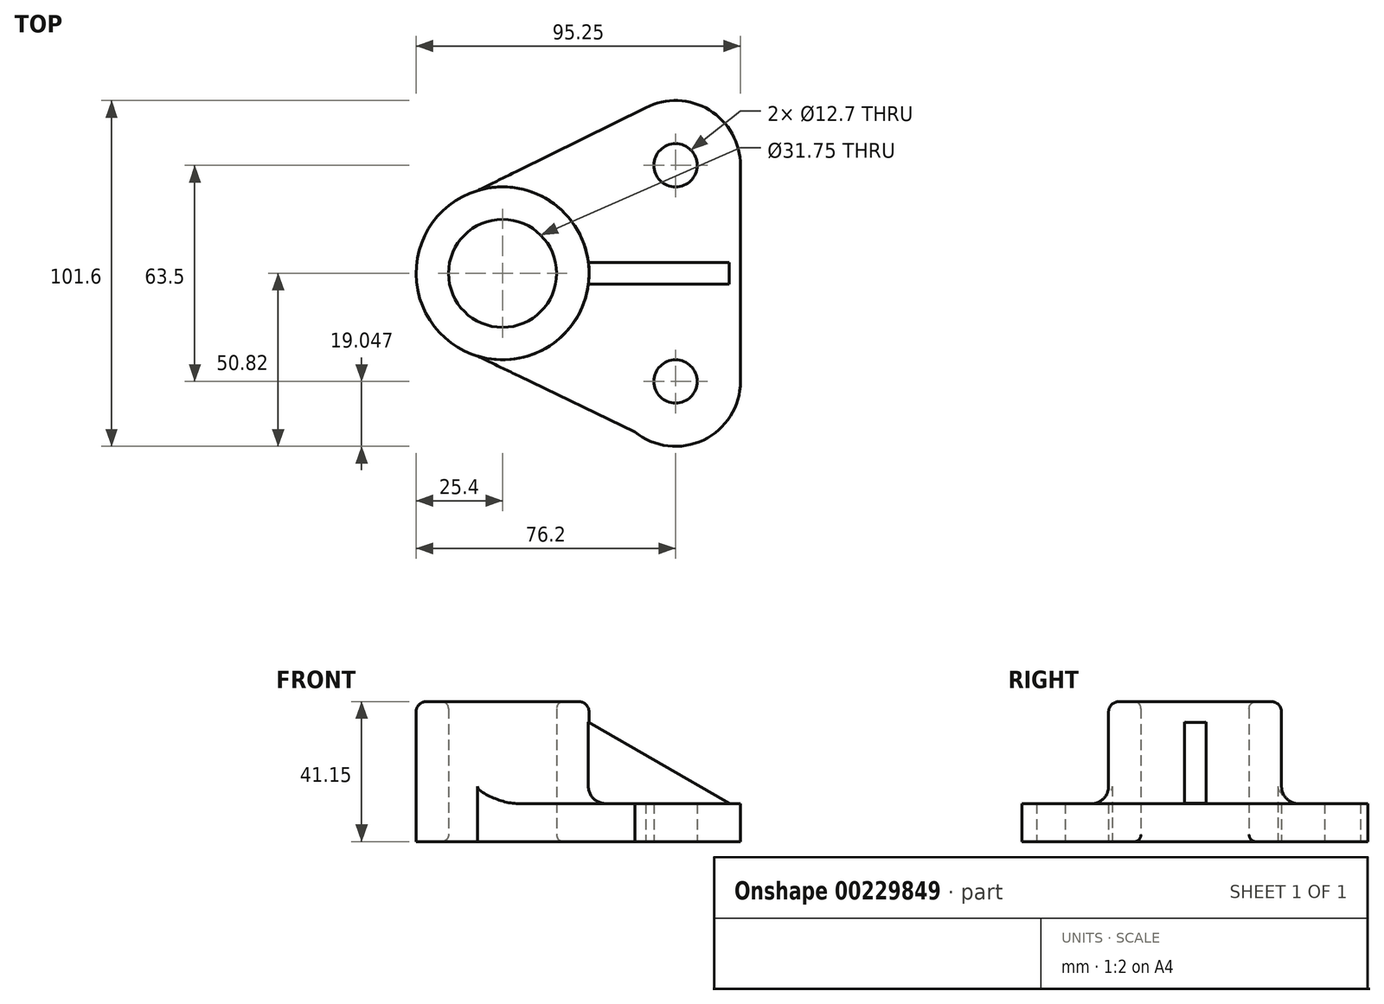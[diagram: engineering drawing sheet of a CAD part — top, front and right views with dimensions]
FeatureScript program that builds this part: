
annotation { "Feature Type Name" : "Feature", "Feature Type Description" : "" }
export const myFeature = defineFeature(function(context is Context, id is Id, definition is map)
    precondition{}
    {
        {
            var Q0;
            Q0=qCreatedBy(makeId("Top.planeOp"),FACE);
            var sketch = newSketch(context, id + "F0", { "sketchPlane" : qUnion([Q0])});
            skCircle(sketch, "E0", {"center": v(-50.8, 0) * mm, "radius": 25.4 * mm});
            skCircle(sketch, "E1", {"center": v(0, 31.73) * mm, "radius": 6.35 * mm});
            skCircle(sketch, "E2", {"center": v(0, -31.77) * mm, "radius": 6.35 * mm});
            skCircle(sketch, "E3", {"center": v(-50.8, 0) * mm, "radius": 15.88 * mm});
            skArc(sketch, "E4", {"start": v(-12.58, 46.03) * mm, "mid": v(15.55, 42.73) * mm, "end": v(9.31, 15.1) * mm});
            skArc(sketch, "E5", {"start": v(-10.88, -16.13) * mm, "mid": v(16.88, -40.6) * mm, "end": v(-19.05, -31.77) * mm});
            skLineSegment(sketch, "E6", {"start": v(19.05, -31.77) * mm, "end": v(19.05, 31.8) * mm});
            skLineSegment(sketch, "E7", {"start": v(-11.99, -46.58) * mm, "end": v(-58.2, -24.3) * mm});
            skLineSegment(sketch, "E8", {"start": v(-8.74, 48.65) * mm, "end": v(-58.2, 24.3) * mm});
            skLineSegment(sketch, "E9", {"start": v(19.05, 0.01) * mm, "end": v(15.75, 0.01) * mm});
            skLineSegment(sketch, "E10", {"start": v(15.75, -3.16) * mm, "end": v(15.75, 3.19) * mm});
            skLineSegment(sketch, "E11", {"start": v(15.75, 3.19) * mm, "end": v(-25.6, 3.19) * mm});
            skLineSegment(sketch, "E12", {"start": v(15.75, -3.16) * mm, "end": v(-25.6, -3.16) * mm});
            skSolve(sketch);
        }
        {
            var Q0;
            Q0=makeQuery(id+"F0.imprint","IMPRINT",FACE,{"disambiguationData":[TD([[makeQuery(id+"F0.imprint","IMPRINT",EDGE,{"derivedFrom":sQuery(id+"F0.wireOp",EDGE,"E0")}),1.0]])]});
            extrude(context, id + "F1", {"entities" : qUnion([Q0]), "depth" : 41.15 * mm});
        }
        {
            var Q0;
            Q0 = qSketchRegion(id + "F0", true);
            extrude(context, id + "F2", {"entities" : qUnion([Q0]), "operationType" : NewBodyOperationType.ADD, "depth" : 11.18 * mm});
        }
        {
            var Q0;
            {var subQ0=sQuery(id+"F0.wireOp",EDGE,"E11");Q0=makeQuery(id+"F0.imprint","IMPRINT",FACE,{"disambiguationData":[TD([[makeQuery(id+"F0.imprint","IMPRINT",EDGE,{"derivedFrom":subQ0}),1.0]])]});}
            extrude(context, id + "F3", {"entities" : qUnion([Q0]), "operationType" : NewBodyOperationType.ADD, "depth" : 41 * mm});
        }
        {
            var Q0;
            Q0=makeQuery(id+"F3.opExtrude","CAP_EDGE",EDGE,{"disambiguationData":[OSD([sQuery(id+"F0.wireOp",EDGE,"E10")])],"isStart":false});
            chamfer(context, id + "F4", {"entities" : qUnion([Q0]), "chamferType" : ChamferType.OFFSET_ANGLE, "width" : 51.56 * mm, "oppositeDirection" : false, "angle" : 30 * degree, "tangentPropagation" : true});
        }
        {
            var Q0;
            Q0=makeQuery(id+"F1.opExtrude","CAP_EDGE",EDGE,{"disambiguationData":[OSD([sQuery(id+"F0.wireOp",EDGE,"E0")])],"isStart":false});
            fillet(context, id + "F5", {"entities" : qUnion([Q0]), "radius" : 3.05 * mm, "tangentPropagation" : true, "allowEdgeOverflow" : false});
        }
        {
            var Q0;
            Q0=makeQuery(id+"F1.opExtrude","CAP_EDGE",EDGE,{"disambiguationData":[OSD([sQuery(id+"F0.wireOp",EDGE,"E3")])],"isStart":true});
            var Q1;
            Q1=makeQuery(id+"F1.opExtrude","CAP_EDGE",EDGE,{"disambiguationData":[OSD([sQuery(id+"F0.wireOp",EDGE,"E3")])],"isStart":false});
            fillet(context, id + "F6", {"entities" : qUnion([Q0, Q1]), "radius" : 2.03 * mm, "tangentPropagation" : true, "allowEdgeOverflow" : false});
        }
        {
            var Q0;
            {var subQ0=sQuery(id+"F0.wireOp",EDGE,"E0");Q0=makeQuery(id+"F2.boolean.opBoolean","INTERSECT",EDGE,{"disambiguationData":[OD(0.0)],"derivedFrom":[makeQuery(id+"F1.opExtrude","SWEPT_FACE",FACE,{"disambiguationData":[OSD([subQ0])]}),makeQuery(id+"F2.opExtrude","CAP_FACE",FACE,{"disambiguationData":[OSD([subQ0,sQuery(id+"F0.wireOp",EDGE,"E1"),sQuery(id+"F0.wireOp",EDGE,"E2"),sQuery(id+"F0.wireOp",EDGE,"E3"),sQuery(id+"F0.wireOp",EDGE,"E4"),sQuery(id+"F0.wireOp",EDGE,"E5"),sQuery(id+"F0.wireOp",EDGE,"E6"),sQuery(id+"F0.wireOp",EDGE,"E7"),sQuery(id+"F0.wireOp",EDGE,"E8"),sQuery(id+"F0.wireOp",EDGE,"E10"),sQuery(id+"F0.wireOp",EDGE,"E11"),sQuery(id+"F0.wireOp",EDGE,"E12")])],"isStart":false})]});}
            var Q1;
            Q1=makeQuery(id+"F2.opExtrude","CAP_EDGE",EDGE,{"disambiguationData":[OSD([sQuery(id+"F0.wireOp",EDGE,"E12")])],"isStart":false});
            var Q2;
            Q2=makeQuery(id+"F3.opExtrude","SWEPT_EDGE",EDGE,{"disambiguationData":[OSD([sQuery(id+"F0.wireOp",EDGE,"E0"),sQuery(id+"F0.wireOp",EDGE,"E12")])]});
            var Q3;
            Q3=makeQuery(id+"F3.opExtrude","SWEPT_EDGE",EDGE,{"disambiguationData":[OSD([sQuery(id+"F0.wireOp",EDGE,"E0"),sQuery(id+"F0.wireOp",EDGE,"E11")])]});
            var Q4;
            {var subQ0=sQuery(id+"F0.wireOp",EDGE,"E0");Q4=makeQuery(id+"F2.boolean.opBoolean","INTERSECT",EDGE,{"disambiguationData":[OD(1.0)],"derivedFrom":[makeQuery(id+"F1.opExtrude","SWEPT_FACE",FACE,{"disambiguationData":[OSD([subQ0])]}),makeQuery(id+"F2.opExtrude","CAP_FACE",FACE,{"disambiguationData":[OSD([subQ0,sQuery(id+"F0.wireOp",EDGE,"E1"),sQuery(id+"F0.wireOp",EDGE,"E2"),sQuery(id+"F0.wireOp",EDGE,"E3"),sQuery(id+"F0.wireOp",EDGE,"E4"),sQuery(id+"F0.wireOp",EDGE,"E5"),sQuery(id+"F0.wireOp",EDGE,"E6"),sQuery(id+"F0.wireOp",EDGE,"E7"),sQuery(id+"F0.wireOp",EDGE,"E8"),sQuery(id+"F0.wireOp",EDGE,"E10"),sQuery(id+"F0.wireOp",EDGE,"E11"),sQuery(id+"F0.wireOp",EDGE,"E12")])],"isStart":false})]});}
            var Q5;
            Q5=makeQuery(id+"F2.opExtrude","CAP_EDGE",EDGE,{"disambiguationData":[OSD([sQuery(id+"F0.wireOp",EDGE,"E11")])],"isStart":false});
            fillet(context, id + "F7", {"entities" : qUnion([Q0, Q1, Q2, Q3, Q4, Q5]), "radius" : 5.08 * mm, "tangentPropagation" : true, "allowEdgeOverflow" : false});
        }
    });
